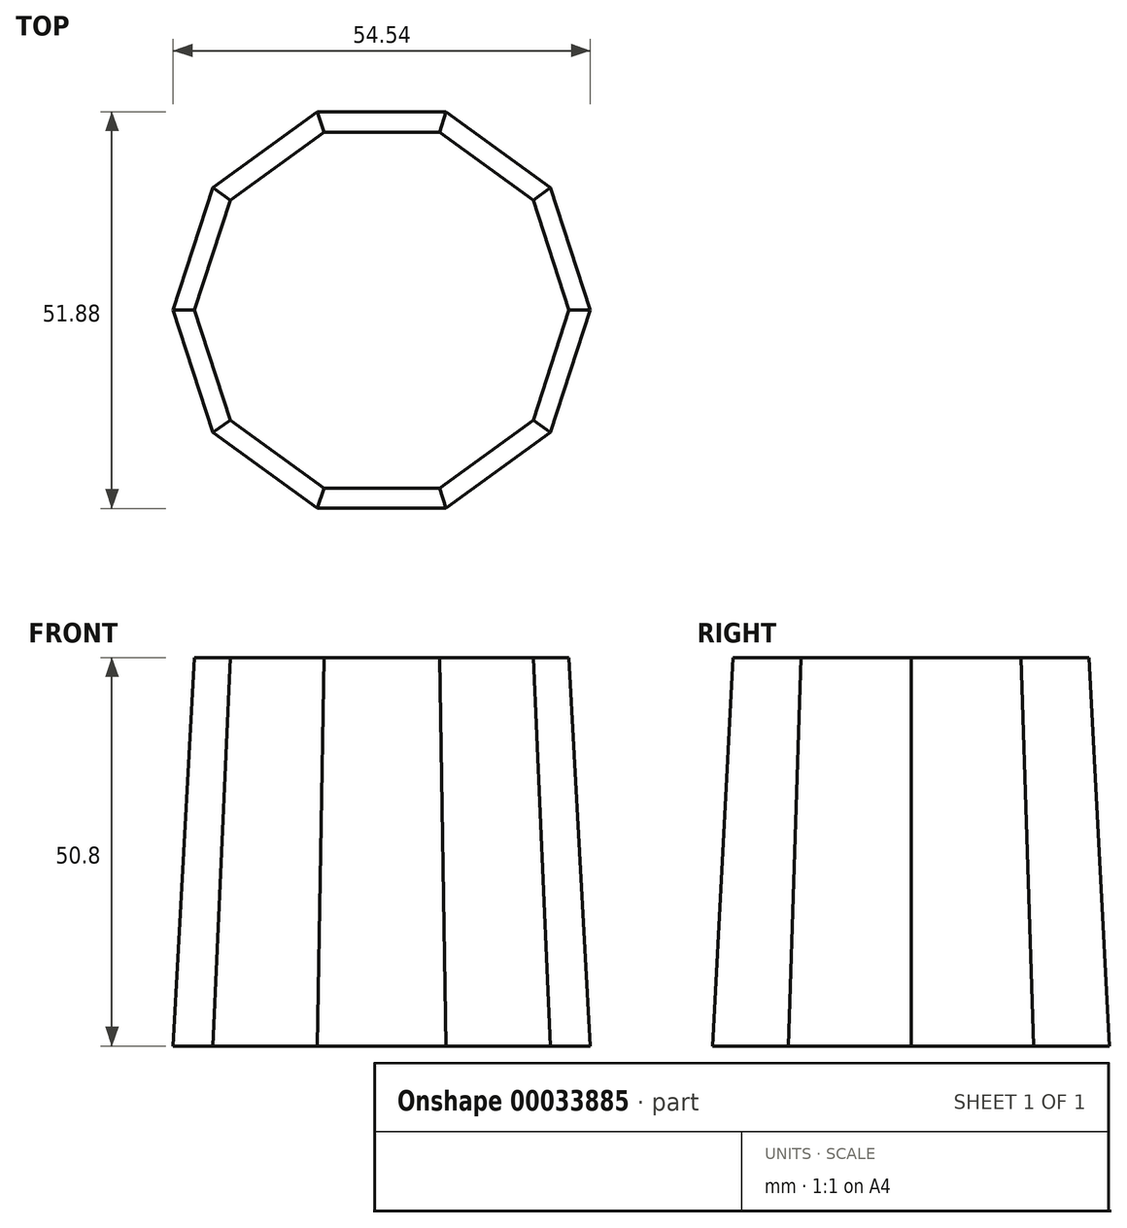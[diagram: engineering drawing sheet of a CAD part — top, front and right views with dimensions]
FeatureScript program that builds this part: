
annotation { "Feature Type Name" : "Feature", "Feature Type Description" : "" }
export const myFeature = defineFeature(function(context is Context, id is Id, definition is map)
    precondition{}
    {
        {
            var Q0;
            Q0=qCreatedBy(makeId("Top.planeOp"),FACE);
            var sketch = newSketch(context, id + "F0", { "sketchPlane" : qUnion([Q0])});
            skCircle(sketch, "E0.cCircle", {"center": v(0, 0) * mm, "radius": 25.94 * mm, "construction": true});
            skLineSegment(sketch, "E0.0", {"start": v(-8.43, 25.94) * mm, "end": v(8.43, 25.94) * mm});
            skLineSegment(sketch, "E0.1", {"start": v(8.43, 25.94) * mm, "end": v(22.06, 16.03) * mm});
            skLineSegment(sketch, "E0.2", {"start": v(22.06, 16.03) * mm, "end": v(27.27, 0) * mm});
            skLineSegment(sketch, "E0.3", {"start": v(27.27, 0) * mm, "end": v(22.06, -16.03) * mm});
            skLineSegment(sketch, "E0.4", {"start": v(22.06, -16.03) * mm, "end": v(8.43, -25.94) * mm});
            skLineSegment(sketch, "E0.5", {"start": v(8.43, -25.94) * mm, "end": v(-8.43, -25.94) * mm});
            skLineSegment(sketch, "E0.6", {"start": v(-8.43, -25.94) * mm, "end": v(-22.06, -16.03) * mm});
            skLineSegment(sketch, "E0.7", {"start": v(-22.06, -16.03) * mm, "end": v(-27.27, 0) * mm});
            skLineSegment(sketch, "E0.8", {"start": v(-27.27, 0) * mm, "end": v(-22.06, 16.03) * mm});
            skLineSegment(sketch, "E0.9", {"start": v(-22.06, 16.03) * mm, "end": v(-8.43, 25.94) * mm});
            skPoint(sketch, "E0.0.midPoint", {"position": v(0, 25.94) * mm});
            skSolve(sketch);
        }
        {
            var Q0;
            Q0=makeQuery(id+"F0.imprint","IMPRINT",FACE,{"disambiguationData":[TD([[makeQuery(id+"F0.imprint","IMPRINT",EDGE,{"derivedFrom":sQuery(id+"F0.wireOp",EDGE,"E0.0")}),-1.0]])]});
            extrude(context, id + "F1", {"entities" : qUnion([Q0]), "depth" : 50.8 * mm, "hasDraft" : true, "draftAngle" : 3 * degree, "draftPullDirection" : true});
        }
    });
